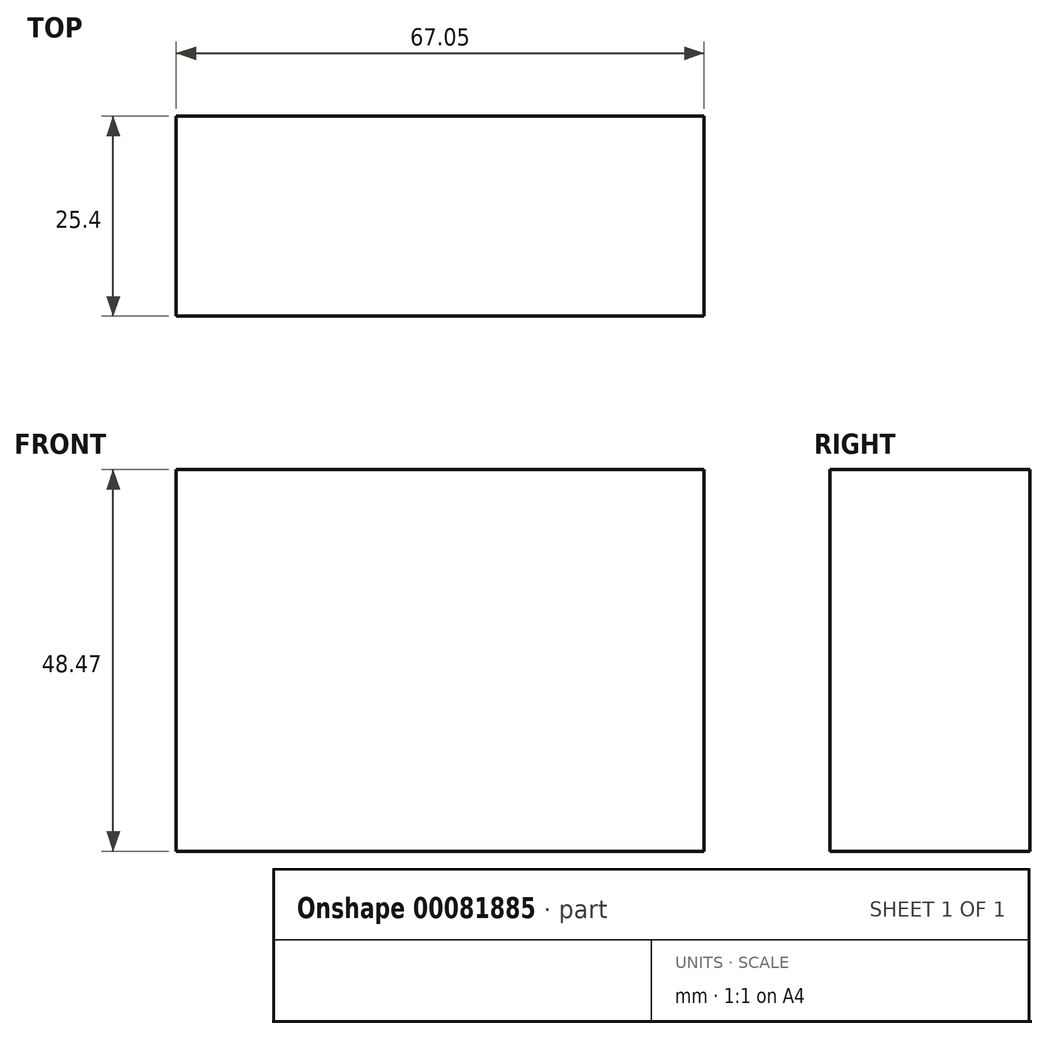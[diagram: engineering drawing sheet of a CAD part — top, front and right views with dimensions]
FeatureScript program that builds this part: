
annotation { "Feature Type Name" : "Feature", "Feature Type Description" : "" }
export const myFeature = defineFeature(function(context is Context, id is Id, definition is map)
    precondition{}
    {
        {
            var Q0;
            Q0=qCreatedBy(makeId("Front.planeOp"),FACE);
            var sketch = newSketch(context, id + "F0", { "sketchPlane" : qUnion([Q0])});
            skLineSegment(sketch, "E0.bottom", {"start": v(-44.06, 63.34) * mm, "end": v(22.99, 63.34) * mm});
            skLineSegment(sketch, "E0.top", {"start": v(-44.06, 14.87) * mm, "end": v(22.99, 14.87) * mm});
            skLineSegment(sketch, "E0.left", {"start": v(-44.06, 63.34) * mm, "end": v(-44.06, 14.87) * mm});
            skLineSegment(sketch, "E0.right", {"start": v(22.99, 63.34) * mm, "end": v(22.99, 14.87) * mm});
            skSolve(sketch);
        }
        {
            var Q0;
            Q0=makeQuery(id+"F0.imprint","IMPRINT",FACE,{"disambiguationData":[TD([[makeQuery(id+"F0.imprint","IMPRINT",EDGE,{"derivedFrom":sQuery(id+"F0.wireOp",EDGE,"E0.bottom")}),-1.0]])]});
            extrude(context, id + "F1", {"entities" : qUnion([Q0]), "depth" : 25.4 * mm});
        }
        {
            var Q0;
            Q0=makeQuery(id+"F1.opExtrude","CAP_FACE",FACE,{"disambiguationData":[OSD([sQuery(id+"F0.wireOp",EDGE,"E0.bottom"),sQuery(id+"F0.wireOp",EDGE,"E0.top"),sQuery(id+"F0.wireOp",EDGE,"E0.left"),sQuery(id+"F0.wireOp",EDGE,"E0.right")])],"isStart":false});
            var sketch = newSketch(context, id + "F2", { "sketchPlane" : qUnion([Q0])});
            skSolve(sketch);
        }
        {
            var Q0;
            Q0=makeQuery(id+"F2.imprint","IMPRINT",FACE,{"disambiguationData":[TD([[makeQuery(id+"F2.imprint","IMPRINT",EDGE,{"derivedFrom":makeQuery(id+"F1.opExtrude","CAP_EDGE",EDGE,{"disambiguationData":[OSD([sQuery(id+"F0.wireOp",EDGE,"E0.bottom")])],"isStart":false})}),-1.0]])]});
            var sketch = newSketch(context, id + "F3", { "sketchPlane" : qUnion([Q0])});
            skLineSegment(sketch, "E1.bottom", {"start": v(-35.15, 51.4) * mm, "end": v(0, 51.4) * mm});
            skLineSegment(sketch, "E1.top", {"start": v(-35.15, 32.84) * mm, "end": v(0, 32.84) * mm});
            skLineSegment(sketch, "E1.left", {"start": v(-35.15, 51.4) * mm, "end": v(-35.15, 32.84) * mm});
            skLineSegment(sketch, "E1.right", {"start": v(0, 51.4) * mm, "end": v(0, 32.84) * mm});
            skSolve(sketch);
        }
        {
            var Q0;
            Q0=sQuery(id+"F3.wireOp",EDGE,"E1.bottom");
            var Q1;
            Q1=sQuery(id+"F3.wireOp",EDGE,"E1.right");
            var Q2;
            Q2=sQuery(id+"F3.wireOp",EDGE,"E1.top");
            var Q3;
            Q3=sQuery(id+"F3.wireOp",EDGE,"E1.left");
            extrude(context, id + "F4", {"bodyType" : ToolBodyType.SURFACE, "surfaceEntities" : qUnion([Q0, Q1, Q2, Q3]), "depth" : 25.4 * mm});
        }
    });
